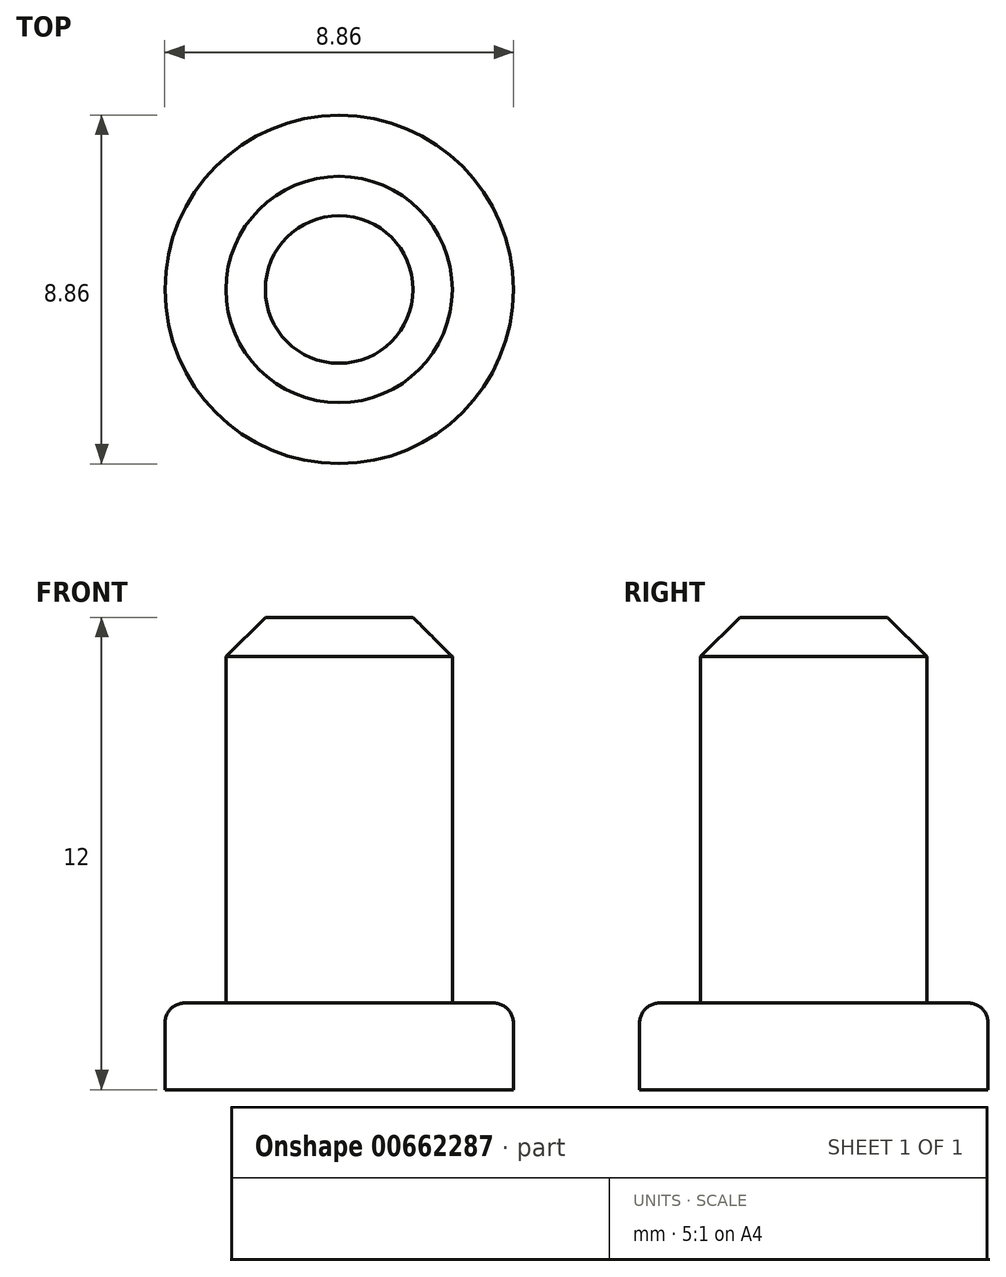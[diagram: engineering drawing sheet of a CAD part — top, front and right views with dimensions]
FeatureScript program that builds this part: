
annotation { "Feature Type Name" : "Feature", "Feature Type Description" : "" }
export const myFeature = defineFeature(function(context is Context, id is Id, definition is map)
    precondition{}
    {
        {
            var Q0;
            Q0=qCreatedBy(makeId("Top.planeOp"),FACE);
            var sketch = newSketch(context, id + "F0", { "sketchPlane" : qUnion([Q0])});
            skCircle(sketch, "E0", {"center": v(0, 0) * mm, "radius": 4.42 * mm});
            skCircle(sketch, "E1", {"center": v(0, 0) * mm, "radius": 2.88 * mm});
            skSolve(sketch);
        }
        {
            var Q0;
            Q0=makeQuery(id+"F0.imprint","IMPRINT",FACE,{"disambiguationData":[TD([[makeQuery(id+"F0.imprint","IMPRINT",EDGE,{"derivedFrom":sQuery(id+"F0.wireOp",EDGE,"E1")}),1.0]])]});
            extrude(context, id + "F1", {"entities" : qUnion([Q0]), "depth" : 12 * mm, "offsetDistance" : 25 * mm});
        }
        {
            var Q0;
            Q0=makeQuery(id+"F0.imprint","IMPRINT",FACE,{"disambiguationData":[TD([[makeQuery(id+"F0.imprint","IMPRINT",EDGE,{"derivedFrom":sQuery(id+"F0.wireOp",EDGE,"E0")}),1.0]])]});
            extrude(context, id + "F2", {"entities" : qUnion([Q0]), "operationType" : NewBodyOperationType.ADD, "depth" : 2.2 * mm, "offsetDistance" : 25 * mm});
        }
        {
            var Q0;
            Q0=makeQuery(id+"F1.opExtrude","CAP_EDGE",EDGE,{"disambiguationData":[OSD([sQuery(id+"F0.wireOp",EDGE,"E1")])],"isStart":false});
            chamfer(context, id + "F3", {"entities" : qUnion([Q0]), "width" : 1 * mm, "tangentPropagation" : true});
        }
        {
            var Q0;
            Q0=makeQuery(id+"F2.opExtrude","CAP_EDGE",EDGE,{"disambiguationData":[OSD([sQuery(id+"F0.wireOp",EDGE,"E0")])],"isStart":false});
            var Q1;
            Q1=makeQuery(id+"F2.opExtrude","CAP_EDGE",EDGE,{"disambiguationData":[OSD([sQuery(id+"F0.wireOp",EDGE,"E1")])],"isStart":false});
            fillet(context, id + "F4", {"entities" : qUnion([Q0, Q1]), "radius" : .5 * mm, "tangentPropagation" : true, "allowEdgeOverflow" : false});
        }
    });
